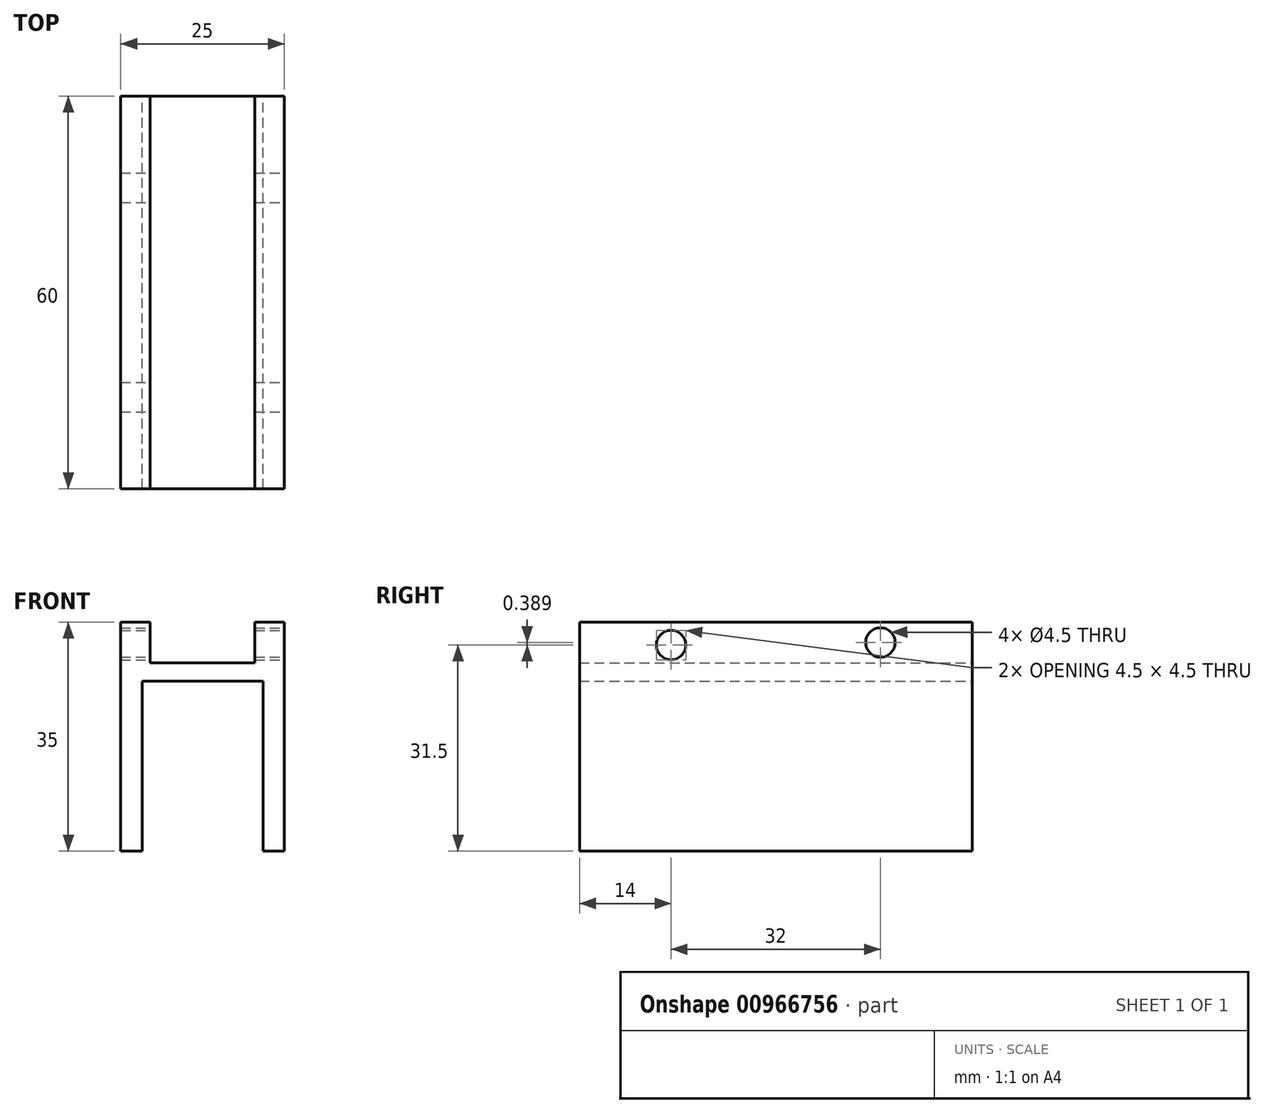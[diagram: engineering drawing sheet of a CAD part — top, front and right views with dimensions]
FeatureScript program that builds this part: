
annotation { "Feature Type Name" : "Feature", "Feature Type Description" : "" }
export const myFeature = defineFeature(function(context is Context, id is Id, definition is map)
    precondition{}
    {
        {
            var Q0;
            Q0=qCreatedBy(makeId("Front.planeOp"),FACE);
            var sketch = newSketch(context, id + "F0", { "sketchPlane" : qUnion([Q0])});
            skLineSegment(sketch, "E0", {"start": v(-8, 1.4) * mm, "end": v(1.25, 1.4) * mm});
            skLineSegment(sketch, "E1", {"start": v(8, 7.6) * mm, "end": v(12.5, 7.6) * mm});
            skLineSegment(sketch, "E2", {"start": v(12.5, 7.6) * mm, "end": v(12.5, -27.4) * mm});
            skLineSegment(sketch, "E3", {"start": v(12.5, -27.4) * mm, "end": v(9.25, -27.4) * mm});
            skLineSegment(sketch, "E4", {"start": v(9.25, -27.4) * mm, "end": v(9.25, -1.4) * mm});
            skLineSegment(sketch, "E5", {"start": v(9.25, -1.4) * mm, "end": v(0, -1.4) * mm});
            skLineSegment(sketch, "E6.MirrorCS", {"start": v(-12.5, -27.4) * mm, "end": v(-9.25, -27.4) * mm});
            skLineSegment(sketch, "E7.MirrorCS", {"start": v(-9.25, -1.4) * mm, "end": v(0, -1.4) * mm});
            skLineSegment(sketch, "E8.MirrorCS", {"start": v(-12.5, 7.6) * mm, "end": v(-12.5, -27.4) * mm});
            skLineSegment(sketch, "E9.MirrorCS", {"start": v(-9.25, -27.4) * mm, "end": v(-9.25, -1.4) * mm});
            skLineSegment(sketch, "E10.MirrorCS", {"start": v(-8, 7.6) * mm, "end": v(-12.5, 7.6) * mm});
            skLineSegment(sketch, "E11.MirrorCS", {"start": v(8, 1.4) * mm, "end": v(-1.25, 1.4) * mm});
            skLineSegment(sketch, "E12", {"start": v(-8, 1.4) * mm, "end": v(-8, 7.6) * mm});
            skLineSegment(sketch, "E13", {"start": v(8, 1.4) * mm, "end": v(8, 7.6) * mm});
            skPoint(sketch, "E14.orphan", {"position": v(0, 7.6) * mm});
            skSolve(sketch);
        }
        {
            var Q0;
            Q0 = qSketchRegion(id + "F0", true);
            extrude(context, id + "F1", {"entities" : qUnion([Q0]), "depth" : 60 * mm, "offsetDistance" : 25 * mm});
        }
        {
            var Q0;
            Q0=makeQuery(id+"F1.opExtrude","SWEPT_FACE",FACE,{"disambiguationData":[OSD([sQuery(id+"F0.wireOp",EDGE,"E2")])]});
            var sketch = newSketch(context, id + "F2", { "sketchPlane" : qUnion([Q0])});
            skPoint(sketch, "E15", {"position": v(-46, 4.1) * mm});
            skPoint(sketch, "E16", {"position": v(-14, 4.49) * mm});
            skSolve(sketch);
        }
        {
            var Q0;
            Q0=sQuery(id+"F2.wireOp",VERTEX,"E15");
            var Q1;
            Q1=sQuery(id+"F2.wireOp",VERTEX,"E16");
            var Q2;
            Q2=makeQuery(id+"F1.opExtrude","SWEPT_BODY",BODY,{"disambiguationData":[OSD([sQuery(id+"F0.wireOp",EDGE,"E0"),sQuery(id+"F0.wireOp",EDGE,"E1"),sQuery(id+"F0.wireOp",EDGE,"E2"),sQuery(id+"F0.wireOp",EDGE,"E3"),sQuery(id+"F0.wireOp",EDGE,"E4"),sQuery(id+"F0.wireOp",EDGE,"E5"),sQuery(id+"F0.wireOp",EDGE,"E6.MirrorCS"),sQuery(id+"F0.wireOp",EDGE,"E7.MirrorCS"),sQuery(id+"F0.wireOp",EDGE,"E8.MirrorCS"),sQuery(id+"F0.wireOp",EDGE,"E9.MirrorCS"),sQuery(id+"F0.wireOp",EDGE,"E10.MirrorCS"),sQuery(id+"F0.wireOp",EDGE,"E11.MirrorCS"),sQuery(id+"F0.wireOp",EDGE,"E12"),sQuery(id+"F0.wireOp",EDGE,"E13")])]});
            hole(context, id + "F3", {"style" : HoleStyle.SIMPLE, "endStyle" : HoleEndStyle.THROUGH, "standardTappedOrClearance" : lookupTablePath({ "fit" : "Normal", "standard" : "ISO", "size" : "M4", "type" : "Clearance" }), "standardBlindInLast" : lookupTablePath({ "fit" : "Normal", "standard" : "ISO", "engagement" : "75%", "pitch" : "0.7 mm", "size" : "M4", "type" : "Clearance & tapped" }), "holeDiameter" : 4.5 * mm, "majorDiameter" : 5 * mm, "isTappedThrough" : true, "tappedDepth" : 12 * mm, "tapClearance" : 3, "locations" : qUnion([Q0, Q1]), "scope" : qUnion([Q2])});
        }
    });
